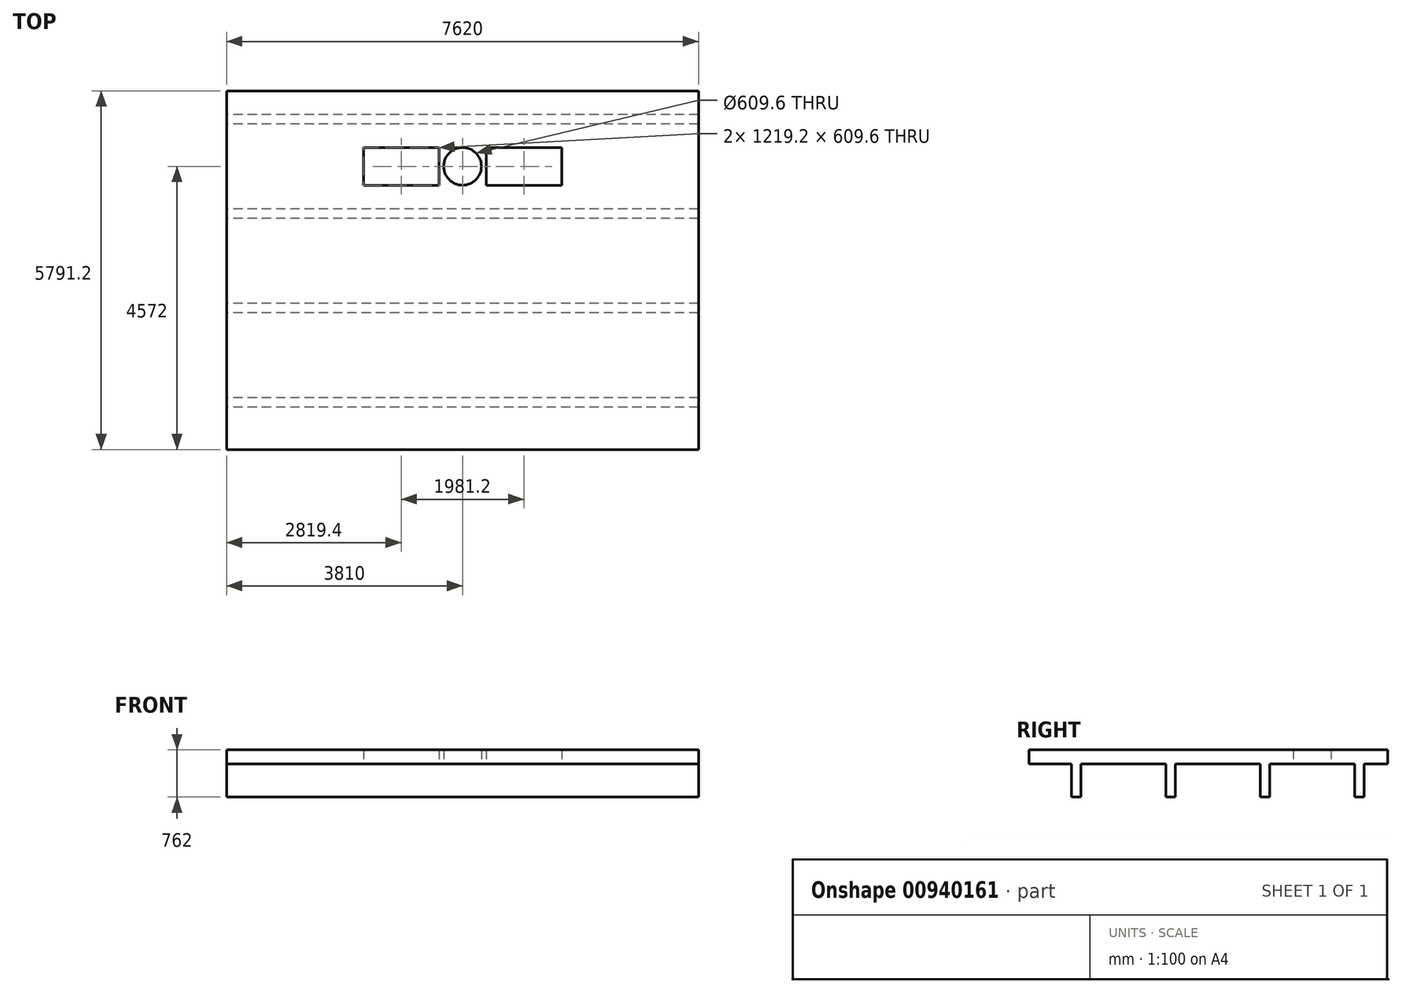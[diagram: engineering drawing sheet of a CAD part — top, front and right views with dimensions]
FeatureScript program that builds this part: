
annotation { "Feature Type Name" : "Feature", "Feature Type Description" : "" }
export const myFeature = defineFeature(function(context is Context, id is Id, definition is map)
    precondition{}
    {
        {
            var Q0;
            Q0=qCreatedBy(makeId("Top.planeOp"),FACE);
            var sketch = newSketch(context, id + "F0", { "sketchPlane" : qUnion([Q0])});
            skLineSegment(sketch, "E0.bottom", {"start": v(-3810, -4572) * mm, "end": v(3810, -4572) * mm});
            skLineSegment(sketch, "E0.top", {"start": v(-3810, 4572) * mm, "end": v(3810, 4572) * mm, "construction": true});
            skLineSegment(sketch, "E0.left", {"start": v(-3810, -4572) * mm, "end": v(-3810, 4572) * mm, "construction": true});
            skLineSegment(sketch, "E0.right", {"start": v(3810, -4572) * mm, "end": v(3810, 4572) * mm, "construction": true});
            skPoint(sketch, "E0.middle", {"position": v(0, 0) * mm});
            skCircle(sketch, "E1", {"center": v(0, 0) * mm, "radius": 304.8 * mm});
            skLineSegment(sketch, "E2.bottom", {"start": v(-1600.2, -304.8) * mm, "end": v(1600.2, -304.8) * mm, "construction": true});
            skLineSegment(sketch, "E2.top", {"start": v(-1600.2, 304.8) * mm, "end": v(1600.2, 304.8) * mm, "construction": true});
            skLineSegment(sketch, "E2.left", {"start": v(-1600.2, -304.8) * mm, "end": v(-1600.2, 304.8) * mm, "construction": true});
            skLineSegment(sketch, "E2.right", {"start": v(1600.2, -304.8) * mm, "end": v(1600.2, 304.8) * mm, "construction": true});
            skLineSegment(sketch, "E3.bottom", {"start": v(-1600.2, 304.8) * mm, "end": v(-381, 304.8) * mm});
            skLineSegment(sketch, "E3.top", {"start": v(-1600.2, -304.8) * mm, "end": v(-381, -304.8) * mm});
            skLineSegment(sketch, "E3.left", {"start": v(-1600.2, 304.8) * mm, "end": v(-1600.2, -304.8) * mm});
            skLineSegment(sketch, "E3.right", {"start": v(-381, 304.8) * mm, "end": v(-381, -304.8) * mm});
            skLineSegment(sketch, "E4.bottom", {"start": v(381, 304.8) * mm, "end": v(1600.2, 304.8) * mm});
            skLineSegment(sketch, "E4.top", {"start": v(381, -304.8) * mm, "end": v(1600.2, -304.8) * mm});
            skLineSegment(sketch, "E4.left", {"start": v(381, 304.8) * mm, "end": v(381, -304.8) * mm});
            skLineSegment(sketch, "E4.right", {"start": v(1600.2, 304.8) * mm, "end": v(1600.2, -304.8) * mm});
            skLineSegment(sketch, "E5", {"start": v(-381, 0) * mm, "end": v(0, 0) * mm});
            skLineSegment(sketch, "E6", {"start": v(381, 0) * mm, "end": v(0, 0) * mm});
            skLineSegment(sketch, "E7.bottom", {"start": v(3810, -4572) * mm, "end": v(-3810, -4572) * mm, "construction": true});
            skLineSegment(sketch, "E7.top", {"start": v(3810, 1219.2) * mm, "end": v(-3810, 1219.2) * mm});
            skLineSegment(sketch, "E7.left", {"start": v(3810, -4572) * mm, "end": v(3810, 1219.2) * mm});
            skLineSegment(sketch, "E7.right", {"start": v(-3810, -4572) * mm, "end": v(-3810, 1219.2) * mm});
            skSolve(sketch);
        }
        {
            var Q0;
            Q0=makeQuery(id+"F0.imprint","IMPRINT",FACE,{"disambiguationData":[TD([[makeQuery(id+"F0.imprint","IMPRINT",EDGE,{"derivedFrom":sQuery(id+"F0.wireOp",EDGE,"E0.bottom")}),1.0]])]});
            extrude(context, id + "F1", {"entities" : qUnion([Q0]), "depth" : 228.6 * mm, "offsetDistance" : 25.4 * mm});
        }
        {
            var Q0;
            Q0=qCreatedBy(makeId("Right.planeOp"),FACE);
            var sketch = newSketch(context, id + "F2", { "sketchPlane" : qUnion([Q0])});
            skLineSegment(sketch, "E8", {"start": v(-685.8, 0) * mm, "end": v(685.8, 0) * mm, "construction": true});
            skLineSegment(sketch, "E9.bottom", {"start": v(-685.8, 0) * mm, "end": v(-838.2, 0) * mm});
            skLineSegment(sketch, "E9.top", {"start": v(-685.8, -533.4) * mm, "end": v(-838.2, -533.4) * mm});
            skLineSegment(sketch, "E9.left", {"start": v(-685.8, 0) * mm, "end": v(-685.8, -533.4) * mm});
            skLineSegment(sketch, "E9.right", {"start": v(-838.2, 0) * mm, "end": v(-838.2, -533.4) * mm});
            skLineSegment(sketch, "E10.bottom", {"start": v(685.8, 0) * mm, "end": v(838.2, 0) * mm});
            skLineSegment(sketch, "E10.top", {"start": v(685.8, -533.4) * mm, "end": v(838.2, -533.4) * mm});
            skLineSegment(sketch, "E10.left", {"start": v(685.8, 0) * mm, "end": v(685.8, -533.4) * mm});
            skLineSegment(sketch, "E10.right", {"start": v(838.2, 0) * mm, "end": v(838.2, -533.4) * mm});
            skLineSegment(sketch, "E11.1.0.0", {"start": v(-3886.2, 0) * mm, "end": v(-3886.2, -533.4) * mm});
            skLineSegment(sketch, "E11.1.0.1", {"start": v(-3733.8, 0) * mm, "end": v(-3886.2, 0) * mm});
            skLineSegment(sketch, "E11.1.0.2", {"start": v(-3733.8, 0) * mm, "end": v(-3733.8, -533.4) * mm});
            skLineSegment(sketch, "E11.1.0.3", {"start": v(-3733.8, -533.4) * mm, "end": v(-3886.2, -533.4) * mm});
            skLineSegment(sketch, "E11.1.0.4", {"start": v(-2362.2, -533.4) * mm, "end": v(-2209.8, -533.4) * mm});
            skLineSegment(sketch, "E11.1.0.5", {"start": v(-2209.8, 0) * mm, "end": v(-2209.8, -533.4) * mm});
            skLineSegment(sketch, "E11.1.0.6", {"start": v(-2362.2, 0) * mm, "end": v(-2362.2, -533.4) * mm});
            skLineSegment(sketch, "E11.1.0.7", {"start": v(-2362.2, 0) * mm, "end": v(-2209.8, 0) * mm});
            skLineSegment(sketch, "E11.direction1", {"start": v(-838.2, -533.4) * mm, "end": v(-3849.1, -533.4) * mm, "construction": true});
            skSolve(sketch);
        }
        {
            var Q0;
            Q0=qSketchRegion(id+"F2",true);
            var Q1;
            Q1=makeQuery(id+"F1.opExtrude","SWEPT_FACE",FACE,{"disambiguationData":[OSD([sQuery(id+"F0.wireOp",EDGE,"E7.left")])]});
            var Q2;
            Q2=makeQuery(id+"F1.opExtrude","SWEPT_FACE",FACE,{"disambiguationData":[OSD([sQuery(id+"F0.wireOp",EDGE,"E7.right")])]});
            extrude(context, id + "F3", {"entities" : qUnion([Q0]), "operationType" : NewBodyOperationType.ADD, "endBound" : BoundingType.UP_TO_SURFACE, "depth" : 25.4 * mm, "endBoundEntityFace" : qUnion([Q1]), "offsetDistance" : 25.4 * mm, "hasSecondDirection" : true, "secondDirectionBound" : SecondDirectionBoundingType.UP_TO_SURFACE, "secondDirectionOppositeDirection" : true, "secondDirectionDepth" : 25.4 * mm, "secondDirectionBoundEntityFace" : qUnion([Q2])});
        }
    });
